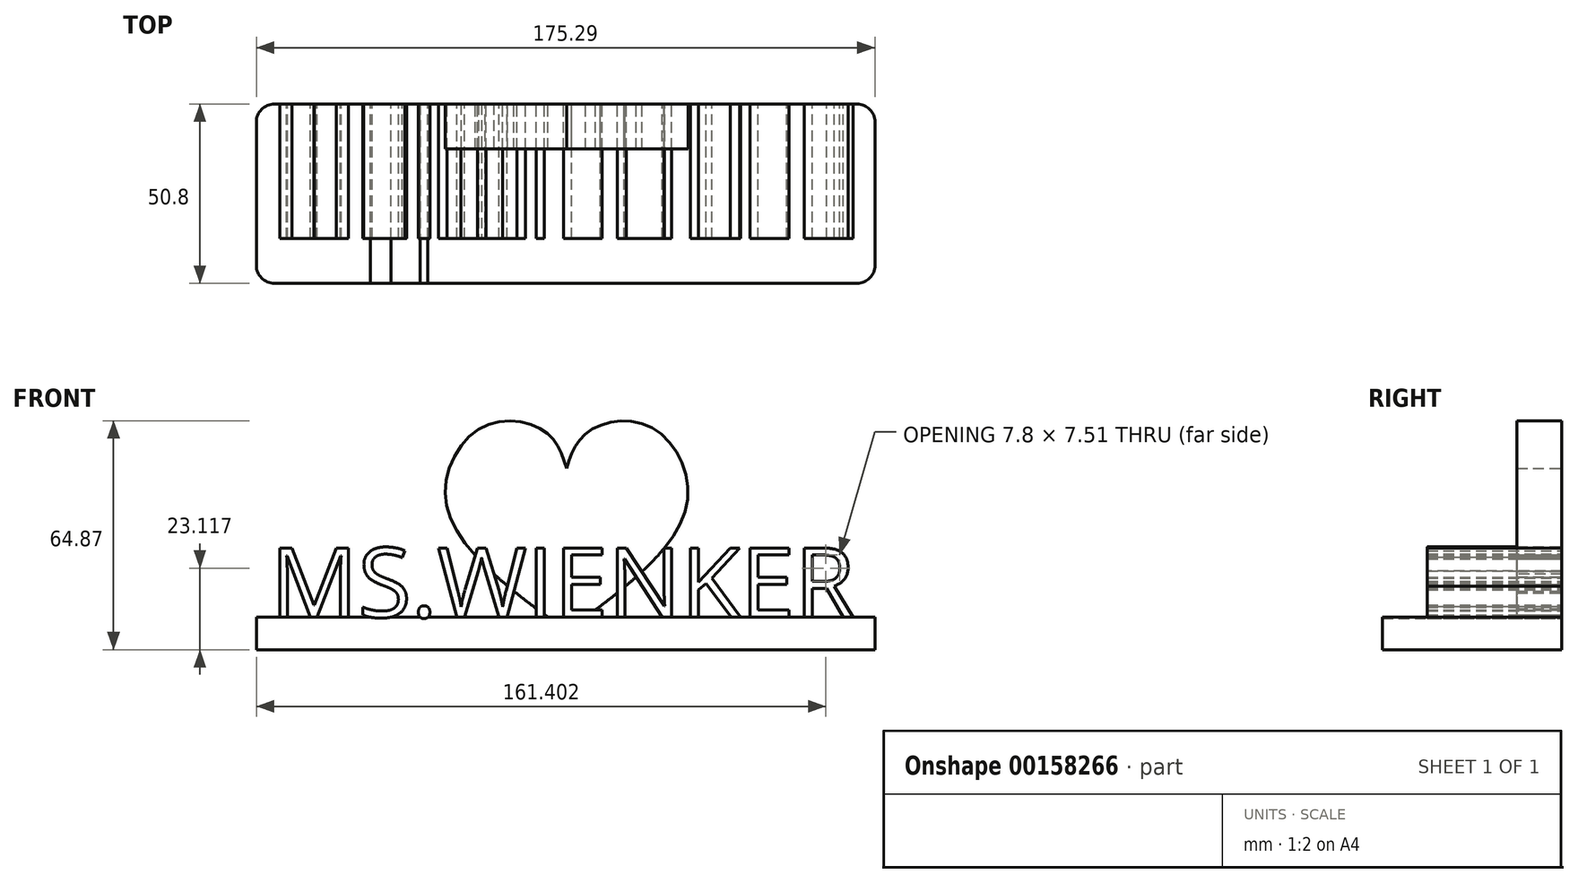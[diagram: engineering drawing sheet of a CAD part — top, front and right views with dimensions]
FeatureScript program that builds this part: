
annotation { "Feature Type Name" : "Feature", "Feature Type Description" : "" }
export const myFeature = defineFeature(function(context is Context, id is Id, definition is map)
    precondition{}
    {
        {
            var Q0;
            Q0=qCreatedBy(makeId("Front.planeOp"),FACE);
            var sketch = newSketch(context, id + "F0", { "sketchPlane" : qUnion([Q0])});
            skLineSegment(sketch, "E0.bottom", {"start": v(-87.93, -17.81) * mm, "end": v(87.36, -17.81) * mm});
            skLineSegment(sketch, "E0.top", {"start": v(-87.93, -27.05) * mm, "end": v(87.36, -27.05) * mm});
            skLineSegment(sketch, "E0.left", {"start": v(-87.93, -17.81) * mm, "end": v(-87.93, -27.05) * mm});
            skLineSegment(sketch, "E0.right", {"start": v(87.36, -17.81) * mm, "end": v(87.36, -27.05) * mm});
            skFitSpline(sketch, "E1", {"points": [v(0, -21.77) * mm, v(-34.11, 14.42) * mm, v(-23.37, 36.28) * mm, v(-5.65, 34.4) * mm, v(0, 24.4) * mm], "startDerivative": vector(-132.98, 97.48) * mm, "endDerivative": vector(20.22, -64.09) * mm});
            skFitSpline(sketch, "E2.MirrorCS", {"points": [v(0, -21.77) * mm, v(34.11, 14.42) * mm, v(23.37, 36.28) * mm, v(5.65, 34.4) * mm, v(0, 24.4) * mm], "startDerivative": vector(132.98, 97.48) * mm, "endDerivative": vector(-20.22, -64.09) * mm});
            skText(sketch, "E3", { "text": "MS.WIENKER", "fontName": "OpenSans-Regular.ttf"});
            const initialGuessF0  = {"E3": [-0.08397, -0.01781, 1, 0, 0.0198]};
            skSetInitialGuess(sketch, initialGuessF0);
            skSolve(sketch);
        }
        {
            var Q0;
            {var subQ0=sQuery(id+"F0.wireOp",EDGE,"E3.sketch_text.stroke-54");Q0=makeQuery(id+"F0.imprint","IMPRINT",FACE,{"disambiguationData":[TD([[makeQuery(id+"F0.imprint","IMPRINT",EDGE,{"derivedFrom":subQ0}),-1.0]])]});}
            var Q1;
            {var subQ5=sQuery(id+"F0.wireOp",EDGE,"E3.sketch_text.stroke-87");Q1=makeQuery(id+"F0.imprint","IMPRINT",FACE,{"disambiguationData":[TD([[makeQuery(id+"F0.imprint","IMPRINT",EDGE,{"derivedFrom":subQ5}),-1.0]])]});}
            var Q2;
            {var subQ1=sQuery(id+"F0.wireOp",EDGE,"E3.sketch_text.stroke-18");Q2=makeQuery(id+"F0.imprint","IMPRINT",FACE,{"disambiguationData":[TD([[makeQuery(id+"F0.imprint","IMPRINT",EDGE,{"derivedFrom":subQ1}),-1.0]])]});}
            var Q3;
            Q3=makeQuery(id+"F0.imprint","IMPRINT",FACE,{"disambiguationData":[TD([[makeQuery(id+"F0.imprint","IMPRINT",EDGE,{"derivedFrom":sQuery(id+"F0.wireOp",EDGE,"E3.sketch_text.stroke-0")}),-1.0]])]});
            var Q4;
            Q4=makeQuery(id+"F0.imprint","IMPRINT",FACE,{"disambiguationData":[TD([[makeQuery(id+"F0.imprint","IMPRINT",EDGE,{"derivedFrom":sQuery(id+"F0.wireOp",EDGE,"E3.sketch_text.stroke-43")}),-1.0]])]});
            var Q5;
            {var subQ0=sQuery(id+"F0.wireOp",EDGE,"E3.sketch_text.stroke-49");var subQ1=sQuery(id+"F0.wireOp",EDGE,"E0.bottom");var subQ2=makeQuery(id+"F0.imprint","INTERSECT",VERTEX,{"derivedFrom":[subQ1,subQ0]});Q5=makeQuery(id+"F0.imprint","IMPRINT",FACE,{"disambiguationData":[TD([[makeQuery(id+"F0.imprint","IMPRINT",EDGE,{"disambiguationData":[TD([[subQ2,-1.0]])],"derivedFrom":subQ1}),-1.0]])]});}
            var Q6;
            {var subQ0=sQuery(id+"F0.wireOp",EDGE,"E3.sketch_text.stroke-20");var subQ1=sQuery(id+"F0.wireOp",EDGE,"E0.bottom");var subQ2=makeQuery(id+"F0.imprint","INTERSECT",VERTEX,{"derivedFrom":[subQ1,subQ0]});Q6=makeQuery(id+"F0.imprint","IMPRINT",FACE,{"disambiguationData":[TD([[makeQuery(id+"F0.imprint","IMPRINT",EDGE,{"disambiguationData":[TD([[subQ2,-1.0]])],"derivedFrom":subQ1}),-1.0]])]});}
            var Q7;
            {var subQ0=sQuery(id+"F0.wireOp",EDGE,"E3.sketch_text.stroke-56");Q7=makeQuery(id+"F0.imprint","IMPRINT",FACE,{"disambiguationData":[TD([[makeQuery(id+"F0.imprint","IMPRINT",EDGE,{"derivedFrom":subQ0}),-1.0]])]});}
            var Q8;
            {var subQ1=sQuery(id+"F0.wireOp",EDGE,"E3.sketch_text.stroke-51");Q8=makeQuery(id+"F0.imprint","IMPRINT",FACE,{"disambiguationData":[TD([[makeQuery(id+"F0.imprint","IMPRINT",EDGE,{"derivedFrom":subQ1}),-1.0]])]});}
            var Q9;
            {var subQ5=sQuery(id+"F0.wireOp",EDGE,"E3.sketch_text.stroke-69");Q9=makeQuery(id+"F0.imprint","IMPRINT",FACE,{"disambiguationData":[TD([[makeQuery(id+"F0.imprint","IMPRINT",EDGE,{"derivedFrom":subQ5}),-1.0]])]});}
            var Q10;
            {var subQ5=sQuery(id+"F0.wireOp",EDGE,"E3.sketch_text.stroke-72");Q10=makeQuery(id+"F0.imprint","IMPRINT",FACE,{"disambiguationData":[TD([[makeQuery(id+"F0.imprint","IMPRINT",EDGE,{"derivedFrom":subQ5}),-1.0]])]});}
            var Q11;
            {var subQ5=sQuery(id+"F0.wireOp",EDGE,"E3.sketch_text.stroke-74");Q11=makeQuery(id+"F0.imprint","IMPRINT",FACE,{"disambiguationData":[TD([[makeQuery(id+"F0.imprint","IMPRINT",EDGE,{"derivedFrom":subQ5}),-1.0]])]});}
            var Q12;
            {var subQ0=sQuery(id+"F0.wireOp",EDGE,"E3.sketch_text.stroke-76");Q12=makeQuery(id+"F0.imprint","IMPRINT",FACE,{"disambiguationData":[TD([[makeQuery(id+"F0.imprint","IMPRINT",EDGE,{"derivedFrom":subQ0}),-1.0]])]});}
            var Q13;
            {var subQ5=sQuery(id+"F0.wireOp",EDGE,"E3.sketch_text.stroke-86");Q13=makeQuery(id+"F0.imprint","IMPRINT",FACE,{"disambiguationData":[TD([[makeQuery(id+"F0.imprint","IMPRINT",EDGE,{"derivedFrom":subQ5}),-1.0]])]});}
            var Q14;
            {var subQ5=sQuery(id+"F0.wireOp",EDGE,"E3.sketch_text.stroke-92");Q14=makeQuery(id+"F0.imprint","IMPRINT",FACE,{"disambiguationData":[TD([[makeQuery(id+"F0.imprint","IMPRINT",EDGE,{"derivedFrom":subQ5}),-1.0]])]});}
            var Q15;
            {var subQ0=sQuery(id+"F0.wireOp",EDGE,"E3.sketch_text.stroke-89");Q15=makeQuery(id+"F0.imprint","IMPRINT",FACE,{"disambiguationData":[TD([[makeQuery(id+"F0.imprint","IMPRINT",EDGE,{"derivedFrom":subQ0}),-1.0]])]});}
            var Q16;
            Q16=makeQuery(id+"F0.imprint","IMPRINT",FACE,{"disambiguationData":[TD([[makeQuery(id+"F0.imprint","IMPRINT",EDGE,{"derivedFrom":sQuery(id+"F0.wireOp",EDGE,"E3.sketch_text.stroke-102")}),-1.0]])]});
            var Q17;
            Q17=makeQuery(id+"F0.imprint","IMPRINT",FACE,{"disambiguationData":[TD([[makeQuery(id+"F0.imprint","IMPRINT",EDGE,{"derivedFrom":sQuery(id+"F0.wireOp",EDGE,"E3.sketch_text.stroke-114")}),-1.0]])]});
            var Q18;
            Q18=makeQuery(id+"F0.imprint","IMPRINT",FACE,{"disambiguationData":[TD([[makeQuery(id+"F0.imprint","IMPRINT",EDGE,{"derivedFrom":sQuery(id+"F0.wireOp",EDGE,"E3.sketch_text.stroke-126")}),-1.0]])]});
            extrude(context, id + "F1", {"entities" : qUnion([Q0, Q1, Q2, Q3, Q4, Q5, Q6, Q7, Q8, Q9, Q10, Q11, Q12, Q13, Q14, Q15, Q16, Q17, Q18]), "depth" : 38.1 * mm});
        }
        {
            var Q0;
            {var subQ14=sQuery(id+"F0.wireOp",EDGE,"E3.sketch_text.stroke-64");Q0=makeQuery(id+"F0.imprint","IMPRINT",FACE,{"disambiguationData":[TD([[makeQuery(id+"F0.imprint","IMPRINT",EDGE,{"derivedFrom":subQ14}),1.0]])]});}
            var Q1;
            {var subQ0=sQuery(id+"F0.wireOp",EDGE,"E3.sketch_text.stroke-89");Q1=makeQuery(id+"F0.imprint","IMPRINT",FACE,{"disambiguationData":[TD([[makeQuery(id+"F0.imprint","IMPRINT",EDGE,{"derivedFrom":subQ0}),1.0]])]});}
            extrude(context, id + "F2", {"entities" : qUnion([Q0, Q1]), "depth" : 12.7 * mm});
        }
        {
            var Q0;
            {var subQ3=sQuery(id+"F0.wireOp",EDGE,"E1");var subQ5=sQuery(id+"F0.wireOp",EDGE,"E2.MirrorCS");var subQ6=makeQuery(id+"F0.imprint","INTERSECT",VERTEX,{"disambiguationData":[OD(0.0)],"derivedFrom":[subQ3,subQ5]});Q0=makeQuery(id+"F0.imprint","IMPRINT",FACE,{"disambiguationData":[TD([[makeQuery(id+"F0.imprint","IMPRINT",EDGE,{"disambiguationData":[TD([[subQ6,-1.0]])],"derivedFrom":subQ3}),-1.0]])]});}
            var Q1;
            Q1=makeQuery(id+"F0.imprint","IMPRINT",FACE,{"disambiguationData":[TD([[makeQuery(id+"F0.imprint","IMPRINT",EDGE,{"derivedFrom":sQuery(id+"F0.wireOp",EDGE,"E0.top")}),1.0]])]});
            extrude(context, id + "F3", {"entities" : qUnion([Q0, Q1]), "depth" : 50.8 * mm});
        }
        {
            var Q0;
            Q0=makeQuery(id+"F3.opExtrude","CAP_EDGE",EDGE,{"disambiguationData":[OSD([sQuery(id+"F0.wireOp",EDGE,"E0.left")])],"isStart":false});
            var Q1;
            Q1=makeQuery(id+"F3.opExtrude","CAP_EDGE",EDGE,{"disambiguationData":[OSD([sQuery(id+"F0.wireOp",EDGE,"E0.right")])],"isStart":false});
            var Q2;
            Q2=makeQuery(id+"F3.opExtrude","CAP_EDGE",EDGE,{"disambiguationData":[OSD([sQuery(id+"F0.wireOp",EDGE,"E0.right")])],"isStart":true});
            var Q3;
            Q3=makeQuery(id+"F3.opExtrude","CAP_EDGE",EDGE,{"disambiguationData":[OSD([sQuery(id+"F0.wireOp",EDGE,"E0.left")])],"isStart":true});
            fillet(context, id + "F4", {"entities" : qUnion([Q0, Q1, Q2, Q3]), "radius" : 5.08 * mm, "tangentPropagation" : true, "allowEdgeOverflow" : false});
        }
    });
